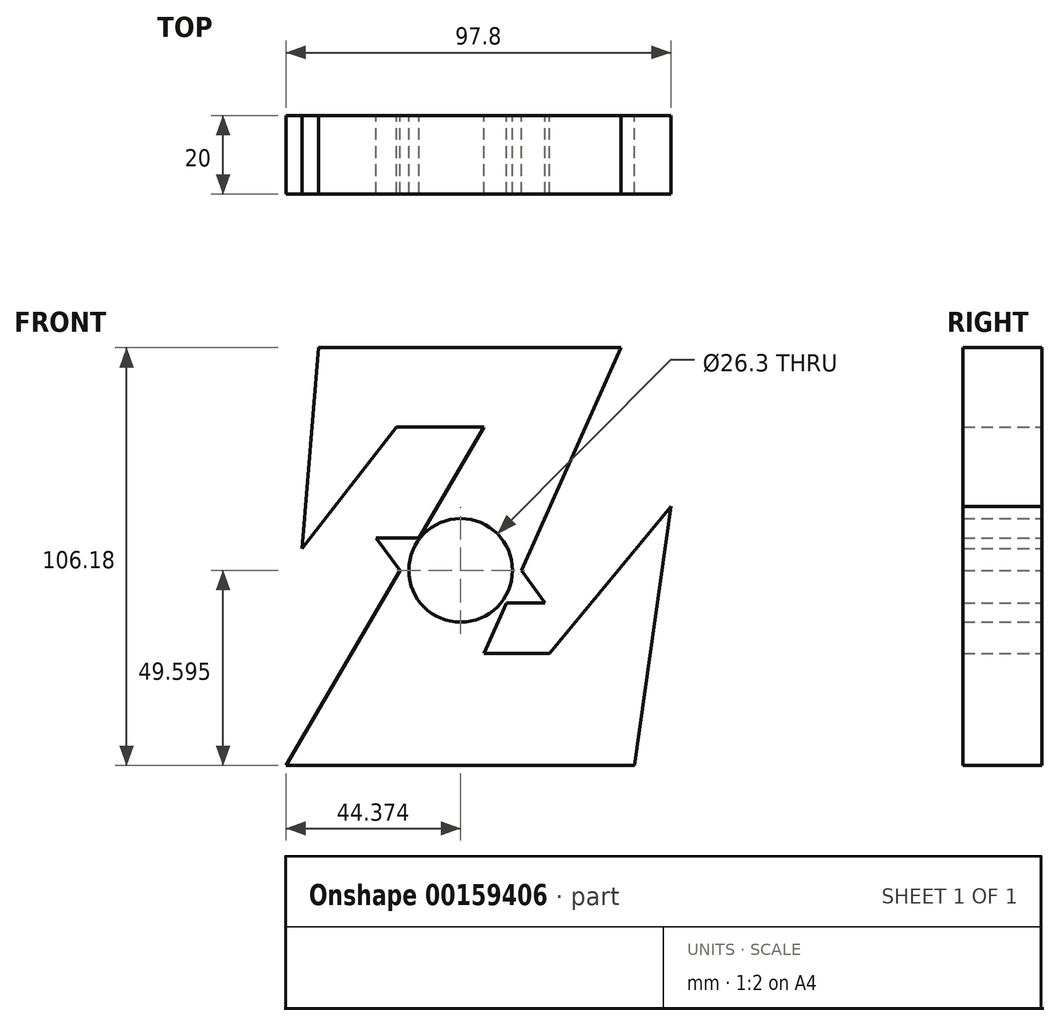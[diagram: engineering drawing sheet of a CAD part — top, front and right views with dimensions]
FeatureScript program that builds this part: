
annotation { "Feature Type Name" : "Feature", "Feature Type Description" : "" }
export const myFeature = defineFeature(function(context is Context, id is Id, definition is map)
    precondition{}
    {
        {
            var Q0;
            Q0=qCreatedBy(makeId("Front.planeOp"),FACE);
            var sketch = newSketch(context, id + "F0", { "sketchPlane" : qUnion([Q0])});
            skLineSegment(sketch, "E0", {"start": v(-46.2, 5.3) * mm, "end": v(-42.1, 56.35) * mm});
            skLineSegment(sketch, "E1", {"start": v(-42.1, 56.35) * mm, "end": v(34.84, 56.35) * mm});
            skLineSegment(sketch, "E2", {"start": v(34.84, 56.35) * mm, "end": v(0, -21.33) * mm});
            skLineSegment(sketch, "E3", {"start": v(0, -21.33) * mm, "end": v(16.58, -21.33) * mm});
            skLineSegment(sketch, "E4", {"start": v(16.58, -21.33) * mm, "end": v(47.5, 15.93) * mm});
            skLineSegment(sketch, "E5", {"start": v(47.5, 15.93) * mm, "end": v(38.19, -49.83) * mm});
            skLineSegment(sketch, "E6", {"start": v(38.19, -49.83) * mm, "end": v(-50.3, -49.83) * mm});
            skLineSegment(sketch, "E7", {"start": v(-50.3, -49.83) * mm, "end": v(0, 36.23) * mm});
            skLineSegment(sketch, "E8", {"start": v(0, 36.23) * mm, "end": v(-22.17, 36.23) * mm});
            skLineSegment(sketch, "E9", {"start": v(-22.17, 36.23) * mm, "end": v(-46.2, 5.3) * mm});
            skLineSegment(sketch, "E10", {"start": v(-16.54, 7.94) * mm, "end": v(-27.38, 7.94) * mm});
            skLineSegment(sketch, "E11", {"start": v(-27.38, 7.94) * mm, "end": v(-21.31, -0.24) * mm});
            skLineSegment(sketch, "E12", {"start": v(-21.31, -0.24) * mm, "end": v(9.46, -0.24) * mm, "construction": true});
            skLineSegment(sketch, "E13", {"start": v(9.46, -0.24) * mm, "end": v(15.46, -8.48) * mm});
            skLineSegment(sketch, "E14", {"start": v(15.46, -8.48) * mm, "end": v(5.73, -8.54) * mm});
            skCircle(sketch, "E15", {"center": v(-5.93, -0.24) * mm, "radius": 13.15 * mm});
            skSolve(sketch);
        }
        {
            var Q0;
            Q0=makeQuery(id+"F0.imprint","IMPRINT",FACE,{"disambiguationData":[TD([[makeQuery(id+"F0.imprint","IMPRINT",EDGE,{"derivedFrom":sQuery(id+"F0.wireOp",EDGE,"E0")}),-1.0]])]});
            var Q1;
            {var subQ0=sQuery(id+"F0.wireOp",EDGE,"E10");Q1=makeQuery(id+"F0.imprint","IMPRINT",FACE,{"disambiguationData":[TD([[makeQuery(id+"F0.imprint","IMPRINT",EDGE,{"derivedFrom":subQ0}),1.0]])]});}
            var Q2;
            {var subQ0=sQuery(id+"F0.wireOp",EDGE,"E13");Q2=makeQuery(id+"F0.imprint","IMPRINT",FACE,{"disambiguationData":[TD([[makeQuery(id+"F0.imprint","IMPRINT",EDGE,{"derivedFrom":subQ0}),-1.0]])]});}
            extrude(context, id + "F1", {"entities" : qUnion([Q0, Q1, Q2]), "depth" : 20 * mm});
        }
    });
